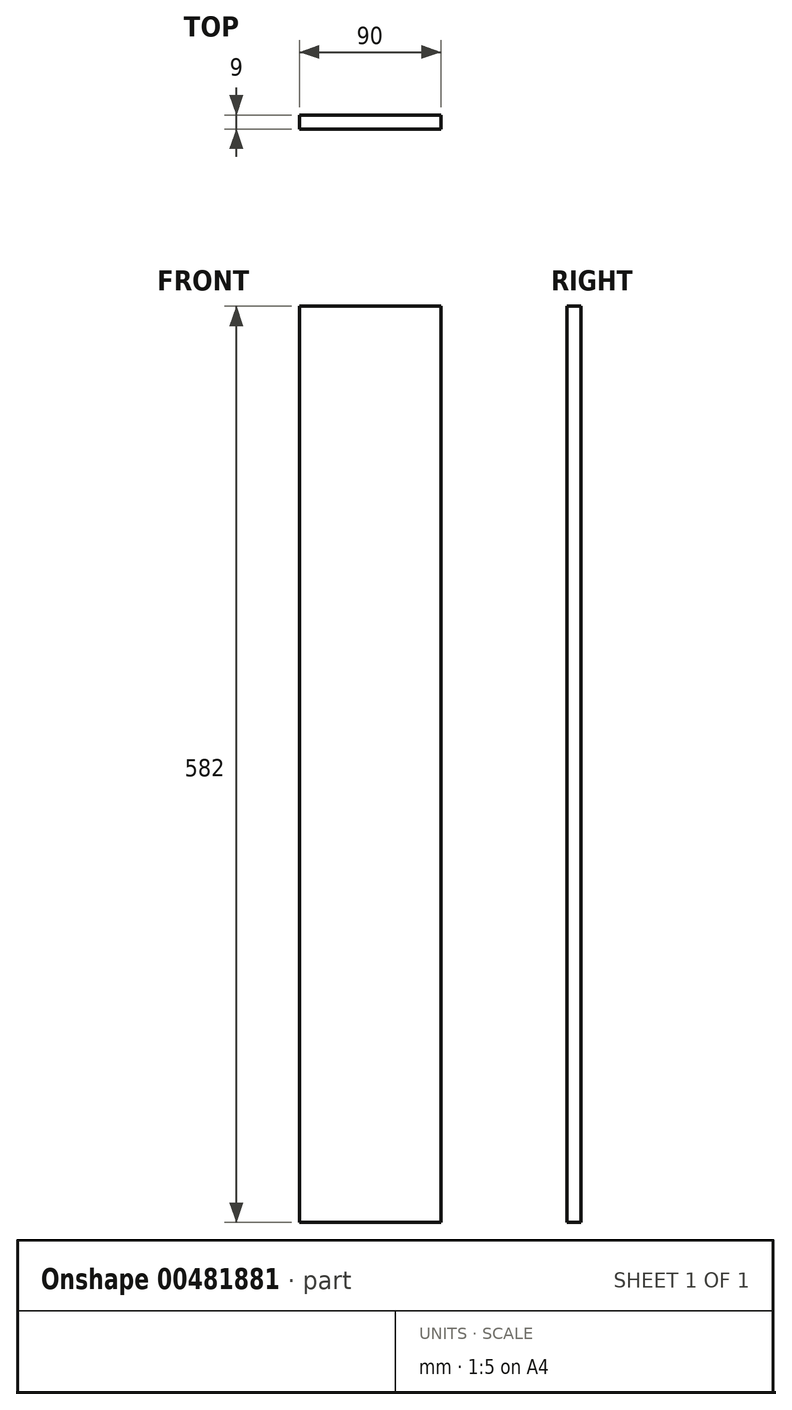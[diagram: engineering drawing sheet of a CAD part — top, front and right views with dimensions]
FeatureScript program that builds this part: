
annotation { "Feature Type Name" : "Feature", "Feature Type Description" : "" }
export const myFeature = defineFeature(function(context is Context, id is Id, definition is map)
    precondition{}
    {
        {
            var Q0;
            Q0=qCreatedBy(makeId("Front.planeOp"),FACE);
            var sketch = newSketch(context, id + "F0", { "sketchPlane" : qUnion([Q0])});
            skLineSegment(sketch, "E0.bottom", {"start": v(0, 0) * mm, "end": v(90, 0) * mm});
            skLineSegment(sketch, "E0.top", {"start": v(0, 582) * mm, "end": v(90, 582) * mm});
            skLineSegment(sketch, "E0.left", {"start": v(0, 0) * mm, "end": v(0, 582) * mm});
            skLineSegment(sketch, "E0.right", {"start": v(90, 0) * mm, "end": v(90, 582) * mm});
            skSolve(sketch);
        }
        {
            var Q0;
            Q0 = qSketchRegion(id + "F0", true);
            extrude(context, id + "F1", {"entities" : qUnion([Q0]), "oppositeDirection" : true, "depth" : 9 * mm});
        }
    });
